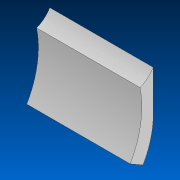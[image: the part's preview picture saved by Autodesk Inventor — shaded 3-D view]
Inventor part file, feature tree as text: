
AUTODESK INVENTOR PART (.ipt)
format: ipt  version: 2022 (Build 260153000, 153)  size: 127,488 bytes
history: native  units: in
note: dims shown in document units (in); Inventor stores cm internally (conversion verified against a paired STEP export)
features: sketch x2, extrude x1, hole x1, pattern_linear x1
ambient origin geometry x8: Origin, YZ Plane, XZ Plane, XY Plane, X Axis, Y Axis, Z Axis, Center Point
bodies: Solid1 (feature_tree)
feature tree (5):
  extrude  "Extrusion1"  Depth=1.0in
  hole  "Hole1"  [1 undecoded]
  pattern_linear  "Rectangular Pattern1"  Spacing1=1.5in  [1 undecoded]
  sketch  "Sketch1"  dims[d0=3.0in d1=1.0in]
  sketch  "Sketch2"  dims[d2=60.0deg d3=1.625in d4=1.5in d5=5.7814in d6=0.817in d7=9.0in d8=3.5in d9=7.0in d10=0.0in d11=0.5in d12=1.0in d13=0.175in d14=0.75in d15=0.22in d16=0.325in d17=0.5635in d18=1.5in d19=0.0in d20=2.3622in d22=1.0in d23=0.5in d24=2.5in]
note: 2 required parameter values undecoded (feature->parameter linkage not recoverable at this tier; creation-order binding heuristic only, values carry confidence <= 0.55)
